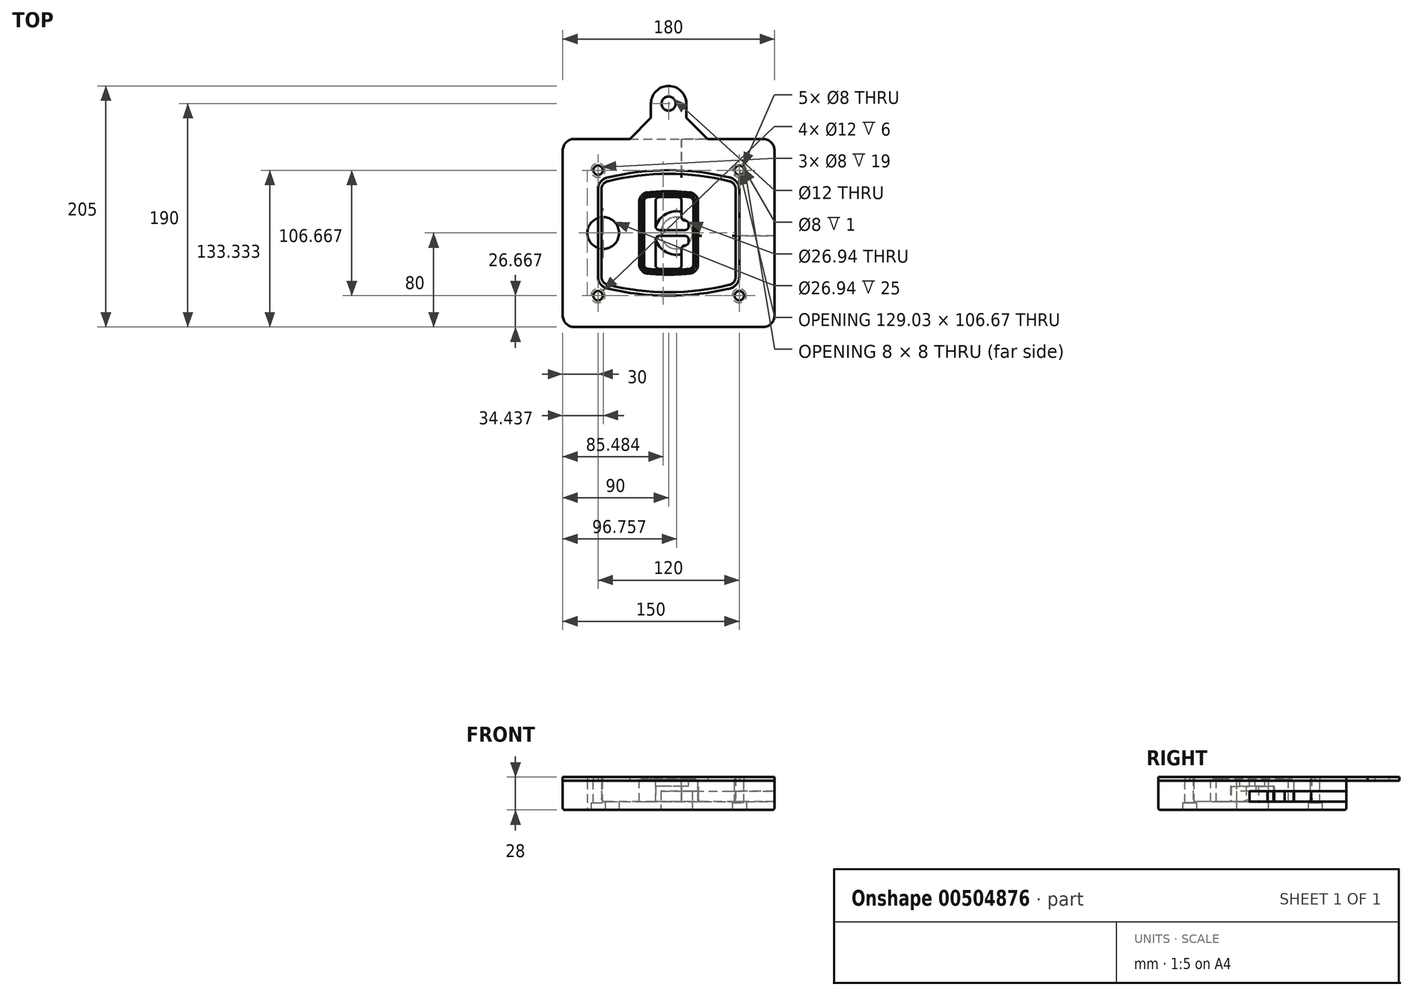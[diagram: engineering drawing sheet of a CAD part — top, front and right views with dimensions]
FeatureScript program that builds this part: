
annotation { "Feature Type Name" : "Feature", "Feature Type Description" : "" }
export const myFeature = defineFeature(function(context is Context, id is Id, definition is map)
    precondition{}
    {
        {
            var Q0;
            Q0=qCreatedBy(makeId("Top.planeOp"),FACE);
            var sketch = newSketch(context, id + "F0", { "sketchPlane" : qUnion([Q0])});
            skPoint(sketch, "E0.rect.middle", {"position": v(0, 0) * mm});
            skLineSegment(sketch, "E1.bottom", {"start": v(-80, -80) * mm, "end": v(80, -80) * mm});
            skLineSegment(sketch, "E1.top", {"start": v(-80, 80) * mm, "end": v(80, 80) * mm});
            skLineSegment(sketch, "E1.left", {"start": v(-90, -70) * mm, "end": v(-90, 70) * mm});
            skLineSegment(sketch, "E1.right", {"start": v(90, -70) * mm, "end": v(90, 70) * mm});
            skLineSegment(sketch, "E2", {"start": v(-90, 80) * mm, "end": v(90, -80) * mm, "construction": true});
            skLineSegment(sketch, "E3", {"start": v(90, 80) * mm, "end": v(-90, -80) * mm, "construction": true});
            skCircle(sketch, "E4", {"center": v(-60, 53.33) * mm, "radius": 4 * mm});
            skCircle(sketch, "E5", {"center": v(60, 53.33) * mm, "radius": 4 * mm});
            skCircle(sketch, "E6", {"center": v(60, -53.33) * mm, "radius": 4 * mm});
            skCircle(sketch, "E7", {"center": v(-60, -53.33) * mm, "radius": 4 * mm});
            skLineSegment(sketch, "E8", {"start": v(-60, 53.33) * mm, "end": v(60, 53.33) * mm, "construction": true});
            skLineSegment(sketch, "E9", {"start": v(60, 53.33) * mm, "end": v(60, -53.33) * mm, "construction": true});
            skLineSegment(sketch, "E10", {"start": v(60, -53.33) * mm, "end": v(-60, -53.33) * mm, "construction": true});
            skLineSegment(sketch, "E11", {"start": v(-60, -53.33) * mm, "end": v(-60, 53.33) * mm, "construction": true});
            skLineSegment(sketch, "E12", {"start": v(-60, 37.3) * mm, "end": v(-60, -37.3) * mm});
            skLineSegment(sketch, "E13", {"start": v(60, 37.3) * mm, "end": v(60, -37.3) * mm});
            skArc(sketch, "E14", {"start": v(52.38, 47.01) * mm, "mid": v(0, 53.33) * mm, "end": v(-52.38, 47.01) * mm});
            skArc(sketch, "E15", {"start": v(-52.38, -47.01) * mm, "mid": v(0, -53.33) * mm, "end": v(52.38, -47.01) * mm});
            skLineSegment(sketch, "E16", {"start": v(-60, 0) * mm, "end": v(60, 0) * mm, "construction": true});
            skPoint(sketch, "E17.visualSharp", {"position": v(-60, -45) * mm});
            skArc(sketch, "E17.filletArc", {"start": v(-60, -37.3) * mm, "mid": v(-57.87, -43.47) * mm, "end": v(-52.38, -47.01) * mm});
            skPoint(sketch, "E18.visualSharp", {"position": v(-60, 45) * mm});
            skArc(sketch, "E18.filletArc", {"start": v(-52.38, 47.01) * mm, "mid": v(-57.87, 43.47) * mm, "end": v(-60, 37.3) * mm});
            skPoint(sketch, "E19.visualSharp", {"position": v(60, 45) * mm});
            skArc(sketch, "E19.filletArc", {"start": v(60, 37.3) * mm, "mid": v(57.87, 43.47) * mm, "end": v(52.38, 47.01) * mm});
            skPoint(sketch, "E20.visualSharp", {"position": v(60, -45) * mm});
            skArc(sketch, "E20.filletArc", {"start": v(52.38, -47.01) * mm, "mid": v(57.87, -43.47) * mm, "end": v(60, -37.3) * mm});
            skPoint(sketch, "E21.visualSharp", {"position": v(-90, 80) * mm});
            skArc(sketch, "E21.filletArc", {"start": v(-80, 80) * mm, "mid": v(-87.07, 77.07) * mm, "end": v(-90, 70) * mm});
            skPoint(sketch, "E22.visualSharp", {"position": v(90, 80) * mm});
            skArc(sketch, "E22.filletArc", {"start": v(90, 70) * mm, "mid": v(87.07, 77.07) * mm, "end": v(80, 80) * mm});
            skPoint(sketch, "E23.visualSharp", {"position": v(90, -80) * mm});
            skArc(sketch, "E23.filletArc", {"start": v(80, -80) * mm, "mid": v(87.07, -77.07) * mm, "end": v(90, -70) * mm});
            skPoint(sketch, "E24.visualSharp", {"position": v(-90, -80) * mm});
            skArc(sketch, "E24.filletArc", {"start": v(-90, -70) * mm, "mid": v(-87.07, -77.07) * mm, "end": v(-80, -80) * mm});
            skArc(sketch, "E25.0", {"start": v(57, 37.3) * mm, "mid": v(55.5, 41.62) * mm, "end": v(51.67, 44.1) * mm});
            skLineSegment(sketch, "E25.1", {"start": v(57, 37.3) * mm, "end": v(57, -37.3) * mm});
            skArc(sketch, "E25.2", {"start": v(51.67, -44.1) * mm, "mid": v(55.5, -41.62) * mm, "end": v(57, -37.3) * mm});
            skArc(sketch, "E25.3", {"start": v(-51.67, -44.1) * mm, "mid": v(0, -50.33) * mm, "end": v(51.67, -44.1) * mm});
            skArc(sketch, "E25.4", {"start": v(-57, -37.3) * mm, "mid": v(-55.5, -41.62) * mm, "end": v(-51.67, -44.1) * mm});
            skArc(sketch, "E25.5", {"start": v(51.67, 44.1) * mm, "mid": v(0, 50.33) * mm, "end": v(-51.67, 44.1) * mm});
            skLineSegment(sketch, "E25.6", {"start": v(-57, 37.3) * mm, "end": v(-57, -37.3) * mm});
            skArc(sketch, "E25.7", {"start": v(-51.67, 44.1) * mm, "mid": v(-55.5, 41.62) * mm, "end": v(-57, 37.3) * mm});
            skArc(sketch, "E26.0", {"start": v(-53.33, 50.9) * mm, "mid": v(-61.01, 45.94) * mm, "end": v(-64, 37.3) * mm});
            skArc(sketch, "E26.1", {"start": v(53.33, 50.9) * mm, "mid": v(0, 57.33) * mm, "end": v(-53.33, 50.9) * mm});
            skArc(sketch, "E26.2", {"start": v(64, 37.3) * mm, "mid": v(61.01, 45.94) * mm, "end": v(53.33, 50.9) * mm});
            skLineSegment(sketch, "E26.3", {"start": v(64, 37.3) * mm, "end": v(64, -37.3) * mm});
            skArc(sketch, "E26.4", {"start": v(53.33, -50.9) * mm, "mid": v(61.01, -45.94) * mm, "end": v(64, -37.3) * mm});
            skLineSegment(sketch, "E26.5", {"start": v(-64, 37.3) * mm, "end": v(-64, -37.3) * mm});
            skArc(sketch, "E26.6", {"start": v(-53.33, -50.9) * mm, "mid": v(0, -57.33) * mm, "end": v(53.33, -50.9) * mm});
            skArc(sketch, "E26.7", {"start": v(-64, -37.3) * mm, "mid": v(-61.01, -45.94) * mm, "end": v(-53.33, -50.9) * mm});
            skSolve(sketch);
        }
        {
            var Q0;
            Q0=makeQuery(id+"F0.imprint","IMPRINT",FACE,{"disambiguationData":[TD([[makeQuery(id+"F0.imprint","IMPRINT",EDGE,{"derivedFrom":sQuery(id+"F0.wireOp",EDGE,"E1.bottom")}),1.0]])]});
            var Q1;
            Q1=makeQuery(id+"F0.imprint","IMPRINT",FACE,{"disambiguationData":[TD([[makeQuery(id+"F0.imprint","IMPRINT",EDGE,{"derivedFrom":sQuery(id+"F0.wireOp",EDGE,"E12")}),1.0]])]});
            var Q2;
            Q2=makeQuery(id+"F0.imprint","IMPRINT",FACE,{"disambiguationData":[TD([[makeQuery(id+"F0.imprint","IMPRINT",EDGE,{"derivedFrom":sQuery(id+"F0.wireOp",EDGE,"E25.0")}),1.0]])]});
            var Q3;
            Q3=makeQuery(id+"F0.imprint","IMPRINT",FACE,{"disambiguationData":[TD([[makeQuery(id+"F0.imprint","IMPRINT",EDGE,{"derivedFrom":sQuery(id+"F0.wireOp",EDGE,"E12")}),-1.0]])]});
            extrude(context, id + "F1", {"entities" : qUnion([Q0, Q1, Q2, Q3]), "oppositeDirection" : true, "depth" : 25 * mm});
        }
        {
            var Q0;
            Q0=makeQuery(id+"F0.imprint","IMPRINT",FACE,{"disambiguationData":[TD([[makeQuery(id+"F0.imprint","IMPRINT",EDGE,{"derivedFrom":sQuery(id+"F0.wireOp",EDGE,"E12")}),1.0]])]});
            extrude(context, id + "F2", {"entities" : qUnion([Q0]), "operationType" : NewBodyOperationType.ADD, "depth" : 3 * mm});
        }
        {
            var Q0;
            Q0=makeQuery(id+"F0.imprint","IMPRINT",FACE,{"disambiguationData":[TD([[makeQuery(id+"F0.imprint","IMPRINT",EDGE,{"derivedFrom":sQuery(id+"F0.wireOp",EDGE,"E25.0")}),1.0]])]});
            extrude(context, id + "F3", {"entities" : qUnion([Q0]), "operationType" : NewBodyOperationType.REMOVE, "oppositeDirection" : true, "depth" : 18 * mm});
        }
        {
            var Q0;
            Q0=makeQuery(id+"F2.opExtrude","CAP_FACE",FACE,{"disambiguationData":[OSD([sQuery(id+"F0.wireOp",EDGE,"E12"),sQuery(id+"F0.wireOp",EDGE,"E13"),sQuery(id+"F0.wireOp",EDGE,"E14"),sQuery(id+"F0.wireOp",EDGE,"E15"),sQuery(id+"F0.wireOp",EDGE,"E17.filletArc"),sQuery(id+"F0.wireOp",EDGE,"E18.filletArc"),sQuery(id+"F0.wireOp",EDGE,"E19.filletArc"),sQuery(id+"F0.wireOp",EDGE,"E20.filletArc"),sQuery(id+"F0.wireOp",EDGE,"E25.0"),sQuery(id+"F0.wireOp",EDGE,"E25.1"),sQuery(id+"F0.wireOp",EDGE,"E25.2"),sQuery(id+"F0.wireOp",EDGE,"E25.3"),sQuery(id+"F0.wireOp",EDGE,"E25.4"),sQuery(id+"F0.wireOp",EDGE,"E25.5"),sQuery(id+"F0.wireOp",EDGE,"E25.6"),sQuery(id+"F0.wireOp",EDGE,"E25.7")])],"isStart":false});
            var sketch = newSketch(context, id + "F4", { "sketchPlane" : qUnion([Q0])});
            skArc(sketch, "E27.0", {"start": v(-17.7, -34.56) * mm, "mid": v(0, -35.33) * mm, "end": v(17.7, -34.56) * mm});
            skArc(sketch, "E28.0", {"start": v(17.7, 34.56) * mm, "mid": v(0, 35.33) * mm, "end": v(-17.7, 34.56) * mm});
            skLineSegment(sketch, "E29", {"start": v(-25, 26.59) * mm, "end": v(-25, -26.59) * mm});
            skLineSegment(sketch, "E30", {"start": v(25, 26.59) * mm, "end": v(25, -26.59) * mm});
            skLineSegment(sketch, "E31", {"start": v(-25, 33.78) * mm, "end": v(25, 33.78) * mm, "construction": true});
            skLineSegment(sketch, "E32", {"start": v(-25, -33.78) * mm, "end": v(25, -33.78) * mm, "construction": true});
            skPoint(sketch, "E33.visualSharp", {"position": v(-25, 33.78) * mm});
            skArc(sketch, "E33.filletArc", {"start": v(-17.7, 34.56) * mm, "mid": v(-22.9, 32) * mm, "end": v(-25, 26.59) * mm});
            skPoint(sketch, "E34.visualSharp", {"position": v(25, 33.78) * mm});
            skArc(sketch, "E34.filletArc", {"start": v(25, 26.59) * mm, "mid": v(22.9, 32) * mm, "end": v(17.7, 34.56) * mm});
            skPoint(sketch, "E35.visualSharp", {"position": v(25, -33.78) * mm});
            skArc(sketch, "E35.filletArc", {"start": v(17.7, -34.56) * mm, "mid": v(22.9, -32) * mm, "end": v(25, -26.59) * mm});
            skPoint(sketch, "E36.visualSharp", {"position": v(-25, -33.78) * mm});
            skArc(sketch, "E36.filletArc", {"start": v(-25, -26.59) * mm, "mid": v(-22.9, -32) * mm, "end": v(-17.7, -34.56) * mm});
            skArc(sketch, "E37.0", {"start": v(51.67, 44.1) * mm, "mid": v(0, 50.33) * mm, "end": v(-51.67, 44.1) * mm});
            skArc(sketch, "E37.1", {"start": v(-51.67, 44.1) * mm, "mid": v(-55.5, 41.62) * mm, "end": v(-57, 37.3) * mm});
            skLineSegment(sketch, "E37.2", {"start": v(-57, 37.3) * mm, "end": v(-57, -37.3) * mm});
            skArc(sketch, "E37.3", {"start": v(-57, -37.3) * mm, "mid": v(-55.5, -41.62) * mm, "end": v(-51.67, -44.1) * mm});
            skArc(sketch, "E37.4", {"start": v(-51.67, -44.1) * mm, "mid": v(0, -50.33) * mm, "end": v(51.67, -44.1) * mm});
            skArc(sketch, "E37.5", {"start": v(51.67, -44.1) * mm, "mid": v(55.5, -41.62) * mm, "end": v(57, -37.3) * mm});
            skLineSegment(sketch, "E37.6", {"start": v(57, 37.3) * mm, "end": v(57, -37.3) * mm});
            skArc(sketch, "E37.7", {"start": v(57, 37.3) * mm, "mid": v(55.5, 41.62) * mm, "end": v(51.67, 44.1) * mm});
            skLineSegment(sketch, "E38.0", {"start": v(23, 26.59) * mm, "end": v(23, -26.59) * mm});
            skArc(sketch, "E38.1", {"start": v(17.53, -32.56) * mm, "mid": v(21.42, -30.64) * mm, "end": v(23, -26.59) * mm});
            skArc(sketch, "E38.2", {"start": v(-17.53, -32.56) * mm, "mid": v(0, -33.33) * mm, "end": v(17.53, -32.56) * mm});
            skArc(sketch, "E38.3", {"start": v(-23, -26.59) * mm, "mid": v(-21.42, -30.64) * mm, "end": v(-17.53, -32.56) * mm});
            skLineSegment(sketch, "E38.4", {"start": v(-23, 26.59) * mm, "end": v(-23, -26.59) * mm});
            skArc(sketch, "E38.5", {"start": v(23, 26.59) * mm, "mid": v(21.42, 30.64) * mm, "end": v(17.53, 32.56) * mm});
            skArc(sketch, "E38.6", {"start": v(-17.53, 32.56) * mm, "mid": v(-21.42, 30.64) * mm, "end": v(-23, 26.59) * mm});
            skArc(sketch, "E38.7", {"start": v(17.53, 32.56) * mm, "mid": v(0, 33.33) * mm, "end": v(-17.53, 32.56) * mm});
            skArc(sketch, "E39.0", {"start": v(21, 26.59) * mm, "mid": v(19.95, 29.29) * mm, "end": v(17.35, 30.57) * mm});
            skLineSegment(sketch, "E39.1", {"start": v(21, 26.59) * mm, "end": v(21, -26.59) * mm});
            skArc(sketch, "E39.2", {"start": v(17.35, -30.57) * mm, "mid": v(19.95, -29.29) * mm, "end": v(21, -26.59) * mm});
            skArc(sketch, "E39.3", {"start": v(-17.35, -30.57) * mm, "mid": v(0, -31.33) * mm, "end": v(17.35, -30.57) * mm});
            skArc(sketch, "E39.4", {"start": v(-21, -26.59) * mm, "mid": v(-19.95, -29.29) * mm, "end": v(-17.35, -30.57) * mm});
            skArc(sketch, "E39.5", {"start": v(17.35, 30.57) * mm, "mid": v(0, 31.33) * mm, "end": v(-17.35, 30.57) * mm});
            skLineSegment(sketch, "E39.6", {"start": v(-21, 26.59) * mm, "end": v(-21, -26.59) * mm});
            skArc(sketch, "E39.7", {"start": v(-17.35, 30.57) * mm, "mid": v(-19.95, 29.29) * mm, "end": v(-21, 26.59) * mm});
            skLineSegment(sketch, "E40", {"start": v(-25, 0) * mm, "end": v(25, 0) * mm, "construction": true});
            skLineSegment(sketch, "E41", {"start": v(-11, 5.5) * mm, "end": v(-11, 27.5) * mm});
            skLineSegment(sketch, "E42", {"start": v(-8, 30.5) * mm, "end": v(8, 30.5) * mm});
            skLineSegment(sketch, "E43", {"start": v(11, 27.5) * mm, "end": v(11, 13.5) * mm});
            skLineSegment(sketch, "E44", {"start": v(14, 10.5) * mm, "end": v(14, 10.5) * mm});
            skLineSegment(sketch, "E45", {"start": v(17, 7.5) * mm, "end": v(17, 5.5) * mm});
            skLineSegment(sketch, "E46", {"start": v(14, 2.5) * mm, "end": v(-8, 2.5) * mm});
            skPoint(sketch, "E47.visualSharp", {"position": v(-11, 30.5) * mm});
            skArc(sketch, "E47.filletArc", {"start": v(-8, 30.5) * mm, "mid": v(-10.12, 29.62) * mm, "end": v(-11, 27.5) * mm});
            skPoint(sketch, "E48.visualSharp", {"position": v(11, 30.5) * mm});
            skArc(sketch, "E48.filletArc", {"start": v(11, 27.5) * mm, "mid": v(10.12, 29.62) * mm, "end": v(8, 30.5) * mm});
            skPoint(sketch, "E49.visualSharp", {"position": v(11, 10.5) * mm});
            skArc(sketch, "E49.filletArc", {"start": v(11, 13.5) * mm, "mid": v(11.88, 11.38) * mm, "end": v(14, 10.5) * mm});
            skPoint(sketch, "E50.visualSharp", {"position": v(17, 10.5) * mm});
            skArc(sketch, "E50.filletArc", {"start": v(17, 7.5) * mm, "mid": v(16.12, 9.62) * mm, "end": v(14, 10.5) * mm});
            skPoint(sketch, "E51.visualSharp", {"position": v(17, 2.5) * mm});
            skArc(sketch, "E51.filletArc", {"start": v(14, 2.5) * mm, "mid": v(16.12, 3.38) * mm, "end": v(17, 5.5) * mm});
            skPoint(sketch, "E52.visualSharp", {"position": v(-11, 2.5) * mm});
            skArc(sketch, "E52.filletArc", {"start": v(-11, 5.5) * mm, "mid": v(-10.12, 3.38) * mm, "end": v(-8, 2.5) * mm});
            skLineSegment(sketch, "E53.0.MirrorCS", {"start": v(14, -2.5) * mm, "end": v(-8, -2.5) * mm});
            skArc(sketch, "E54.0.MirrorCS", {"start": v(-11, -5.5) * mm, "mid": v(-10.12, -3.38) * mm, "end": v(-8, -2.5) * mm});
            skLineSegment(sketch, "E55.0.MirrorCS", {"start": v(-11, -5.5) * mm, "end": v(-11, -27.5) * mm});
            skArc(sketch, "E56.0.MirrorCS", {"start": v(-8, -30.5) * mm, "mid": v(-10.12, -29.62) * mm, "end": v(-11, -27.5) * mm});
            skLineSegment(sketch, "E57.0.MirrorCS", {"start": v(-8, -30.5) * mm, "end": v(8, -30.5) * mm});
            skArc(sketch, "E58.0.MirrorCS", {"start": v(11, -27.5) * mm, "mid": v(10.12, -29.62) * mm, "end": v(8, -30.5) * mm});
            skLineSegment(sketch, "E59.0.MirrorCS", {"start": v(11, -27.5) * mm, "end": v(11, -13.5) * mm});
            skArc(sketch, "E60.0.MirrorCS", {"start": v(11, -13.5) * mm, "mid": v(11.88, -11.38) * mm, "end": v(14, -10.5) * mm});
            skArc(sketch, "E61.0.MirrorCS", {"start": v(17, -7.5) * mm, "mid": v(16.12, -9.62) * mm, "end": v(14, -10.5) * mm});
            skLineSegment(sketch, "E62.0.MirrorCS", {"start": v(17, -7.5) * mm, "end": v(17, -5.5) * mm});
            skArc(sketch, "E63.0.MirrorCS", {"start": v(14, -2.5) * mm, "mid": v(16.12, -3.38) * mm, "end": v(17, -5.5) * mm});
            skSolve(sketch);
        }
        {
            var Q0;
            Q0=makeQuery(id+"F4.imprint","IMPRINT",FACE,{"disambiguationData":[TD([[makeQuery(id+"F4.imprint","IMPRINT",EDGE,{"derivedFrom":sQuery(id+"F4.wireOp",EDGE,"E27.0")}),1.0]])]});
            var Q1;
            Q1=makeQuery(id+"F4.imprint","IMPRINT",FACE,{"disambiguationData":[TD([[makeQuery(id+"F4.imprint","IMPRINT",EDGE,{"derivedFrom":sQuery(id+"F4.wireOp",EDGE,"E38.0")}),-1.0]])]});
            var Q2;
            Q2=makeQuery(id+"F4.imprint","IMPRINT",FACE,{"disambiguationData":[TD([[makeQuery(id+"F4.imprint","IMPRINT",EDGE,{"derivedFrom":sQuery(id+"F4.wireOp",EDGE,"E39.0")}),1.0]])]});
            extrude(context, id + "F5", {"entities" : qUnion([Q0, Q1, Q2]), "operationType" : NewBodyOperationType.ADD, "endBound" : BoundingType.UP_TO_NEXT, "oppositeDirection" : true, "depth" : 25 * mm});
        }
        {
            var Q0;
            Q0=makeQuery(id+"F4.imprint","IMPRINT",FACE,{"disambiguationData":[TD([[makeQuery(id+"F4.imprint","IMPRINT",EDGE,{"derivedFrom":sQuery(id+"F4.wireOp",EDGE,"E38.0")}),-1.0]])]});
            extrude(context, id + "F6", {"entities" : qUnion([Q0]), "operationType" : NewBodyOperationType.REMOVE, "oppositeDirection" : true, "depth" : 2 * mm});
        }
        {
            var Q0;
            Q0=makeQuery(id+"F1.opExtrude","CAP_FACE",FACE,{"disambiguationData":[OSD([sQuery(id+"F0.wireOp",EDGE,"E1.bottom"),sQuery(id+"F0.wireOp",EDGE,"E1.top"),sQuery(id+"F0.wireOp",EDGE,"E1.left"),sQuery(id+"F0.wireOp",EDGE,"E1.right"),sQuery(id+"F0.wireOp",EDGE,"E4"),sQuery(id+"F0.wireOp",EDGE,"E5"),sQuery(id+"F0.wireOp",EDGE,"E6"),sQuery(id+"F0.wireOp",EDGE,"E7"),sQuery(id+"F0.wireOp",EDGE,"E21.filletArc"),sQuery(id+"F0.wireOp",EDGE,"E22.filletArc"),sQuery(id+"F0.wireOp",EDGE,"E23.filletArc"),sQuery(id+"F0.wireOp",EDGE,"E24.filletArc")])],"isStart":false});
            var sketch = newSketch(context, id + "F7", { "sketchPlane" : qUnion([Q0])});
            skCircle(sketch, "E64", {"center": v(6.76, 0) * mm, "radius": 13.47 * mm});
            skCircle(sketch, "E65", {"center": v(-55.56, 0) * mm, "radius": 13.47 * mm});
            skLineSegment(sketch, "E66", {"start": v(90, 0) * mm, "end": v(-90, 0) * mm});
            skCircle(sketch, "E67", {"center": v(6.76, 0) * mm, "radius": 18.47 * mm});
            skCircle(sketch, "E68", {"center": v(60, -53.33) * mm, "radius": 6 * mm});
            skCircle(sketch, "E69", {"center": v(-60, -53.33) * mm, "radius": 6 * mm});
            skCircle(sketch, "E70", {"center": v(-60, 53.33) * mm, "radius": 6 * mm});
            skCircle(sketch, "E71", {"center": v(60, 53.33) * mm, "radius": 6 * mm});
            skSolve(sketch);
        }
        {
            var Q0;
            {var subQ1=sQuery(id+"F7.wireOp",EDGE,"E66");var subQ4=sQuery(id+"F7.wireOp",EDGE,"E64");var subQ6=makeQuery(id+"F7.imprint","INTERSECT",VERTEX,{"disambiguationData":[OD(0.0)],"derivedFrom":[subQ4,subQ1]});Q0=makeQuery(id+"F7.imprint","IMPRINT",FACE,{"disambiguationData":[TD([[makeQuery(id+"F7.imprint","IMPRINT",EDGE,{"disambiguationData":[TD([[subQ6,-1.0]])],"derivedFrom":subQ4}),-1.0]])]});}
            var Q1;
            {var subQ0=sQuery(id+"F7.wireOp",EDGE,"E66");var subQ1=sQuery(id+"F7.wireOp",EDGE,"E64");var subQ3=makeQuery(id+"F7.imprint","INTERSECT",VERTEX,{"disambiguationData":[OD(0.0)],"derivedFrom":[subQ1,subQ0]});Q1=makeQuery(id+"F7.imprint","IMPRINT",FACE,{"disambiguationData":[TD([[makeQuery(id+"F7.imprint","IMPRINT",EDGE,{"disambiguationData":[TD([[subQ3,-1.0]])],"derivedFrom":subQ1}),1.0]])]});}
            var Q2;
            {var subQ0=sQuery(id+"F7.wireOp",EDGE,"E66");var subQ1=sQuery(id+"F7.wireOp",EDGE,"E64");var subQ3=makeQuery(id+"F7.imprint","INTERSECT",VERTEX,{"disambiguationData":[OD(0.0)],"derivedFrom":[subQ1,subQ0]});Q2=makeQuery(id+"F7.imprint","IMPRINT",FACE,{"disambiguationData":[TD([[makeQuery(id+"F7.imprint","IMPRINT",EDGE,{"disambiguationData":[TD([[subQ3,1.0]])],"derivedFrom":subQ1}),1.0]])]});}
            var Q3;
            {var subQ1=sQuery(id+"F7.wireOp",EDGE,"E66");var subQ4=sQuery(id+"F7.wireOp",EDGE,"E64");var subQ6=makeQuery(id+"F7.imprint","INTERSECT",VERTEX,{"disambiguationData":[OD(0.0)],"derivedFrom":[subQ4,subQ1]});Q3=makeQuery(id+"F7.imprint","IMPRINT",FACE,{"disambiguationData":[TD([[makeQuery(id+"F7.imprint","IMPRINT",EDGE,{"disambiguationData":[TD([[subQ6,1.0]])],"derivedFrom":subQ4}),-1.0]])]});}
            extrude(context, id + "F8", {"entities" : qUnion([Q0, Q1, Q2, Q3]), "operationType" : NewBodyOperationType.ADD, "oppositeDirection" : true, "depth" : 20 * mm});
        }
        {
            var Q0;
            {var subQ0=sQuery(id+"F7.wireOp",EDGE,"E66");var subQ1=sQuery(id+"F7.wireOp",EDGE,"E64");var subQ3=makeQuery(id+"F7.imprint","INTERSECT",VERTEX,{"disambiguationData":[OD(0.0)],"derivedFrom":[subQ1,subQ0]});Q0=makeQuery(id+"F7.imprint","IMPRINT",FACE,{"disambiguationData":[TD([[makeQuery(id+"F7.imprint","IMPRINT",EDGE,{"disambiguationData":[TD([[subQ3,-1.0]])],"derivedFrom":subQ1}),1.0]])]});}
            var Q1;
            {var subQ0=sQuery(id+"F7.wireOp",EDGE,"E66");var subQ1=sQuery(id+"F7.wireOp",EDGE,"E64");var subQ3=makeQuery(id+"F7.imprint","INTERSECT",VERTEX,{"disambiguationData":[OD(0.0)],"derivedFrom":[subQ1,subQ0]});Q1=makeQuery(id+"F7.imprint","IMPRINT",FACE,{"disambiguationData":[TD([[makeQuery(id+"F7.imprint","IMPRINT",EDGE,{"disambiguationData":[TD([[subQ3,1.0]])],"derivedFrom":subQ1}),1.0]])]});}
            extrude(context, id + "F9", {"entities" : qUnion([Q0, Q1]), "operationType" : NewBodyOperationType.REMOVE, "oppositeDirection" : true, "depth" : 16 * mm});
        }
        {
            var Q0;
            {var subQ0=sQuery(id+"F7.wireOp",EDGE,"E66");var subQ1=sQuery(id+"F7.wireOp",EDGE,"E65");var subQ3=makeQuery(id+"F7.imprint","INTERSECT",VERTEX,{"disambiguationData":[OD(0.0)],"derivedFrom":[subQ1,subQ0]});Q0=makeQuery(id+"F7.imprint","IMPRINT",FACE,{"disambiguationData":[TD([[makeQuery(id+"F7.imprint","IMPRINT",EDGE,{"disambiguationData":[TD([[subQ3,-1.0]])],"derivedFrom":subQ1}),1.0]])]});}
            var Q1;
            {var subQ0=sQuery(id+"F7.wireOp",EDGE,"E66");var subQ1=sQuery(id+"F7.wireOp",EDGE,"E65");var subQ3=makeQuery(id+"F7.imprint","INTERSECT",VERTEX,{"disambiguationData":[OD(0.0)],"derivedFrom":[subQ1,subQ0]});Q1=makeQuery(id+"F7.imprint","IMPRINT",FACE,{"disambiguationData":[TD([[makeQuery(id+"F7.imprint","IMPRINT",EDGE,{"disambiguationData":[TD([[subQ3,1.0]])],"derivedFrom":subQ1}),1.0]])]});}
            extrude(context, id + "F10", {"entities" : qUnion([Q0, Q1]), "operationType" : NewBodyOperationType.REMOVE, "oppositeDirection" : true, "depth" : 25 * mm});
        }
        {
            var Q0;
            Q0=makeQuery(id+"F7.imprint","IMPRINT",FACE,{"disambiguationData":[TD([[makeQuery(id+"F7.imprint","IMPRINT",EDGE,{"derivedFrom":sQuery(id+"F7.wireOp",EDGE,"E68")}),1.0]])]});
            var Q1;
            Q1=makeQuery(id+"F7.imprint","IMPRINT",FACE,{"disambiguationData":[TD([[makeQuery(id+"F7.imprint","IMPRINT",EDGE,{"derivedFrom":makeQuery(id+"F1.opExtrude","CAP_EDGE",EDGE,{"disambiguationData":[OSD([sQuery(id+"F0.wireOp",EDGE,"E5")])],"isStart":false})}),-1.0]])]});
            var Q2;
            Q2=makeQuery(id+"F7.imprint","IMPRINT",FACE,{"disambiguationData":[TD([[makeQuery(id+"F7.imprint","IMPRINT",EDGE,{"derivedFrom":sQuery(id+"F7.wireOp",EDGE,"E69")}),1.0]])]});
            var Q3;
            Q3=makeQuery(id+"F7.imprint","IMPRINT",FACE,{"disambiguationData":[TD([[makeQuery(id+"F7.imprint","IMPRINT",EDGE,{"derivedFrom":makeQuery(id+"F1.opExtrude","CAP_EDGE",EDGE,{"disambiguationData":[OSD([sQuery(id+"F0.wireOp",EDGE,"E4")])],"isStart":false})}),-1.0]])]});
            var Q4;
            Q4=makeQuery(id+"F7.imprint","IMPRINT",FACE,{"disambiguationData":[TD([[makeQuery(id+"F7.imprint","IMPRINT",EDGE,{"derivedFrom":sQuery(id+"F7.wireOp",EDGE,"E70")}),1.0]])]});
            var Q5;
            Q5=makeQuery(id+"F7.imprint","IMPRINT",FACE,{"disambiguationData":[TD([[makeQuery(id+"F7.imprint","IMPRINT",EDGE,{"derivedFrom":makeQuery(id+"F1.opExtrude","CAP_EDGE",EDGE,{"disambiguationData":[OSD([sQuery(id+"F0.wireOp",EDGE,"E7")])],"isStart":false})}),-1.0]])]});
            var Q6;
            Q6=makeQuery(id+"F7.imprint","IMPRINT",FACE,{"disambiguationData":[TD([[makeQuery(id+"F7.imprint","IMPRINT",EDGE,{"derivedFrom":sQuery(id+"F7.wireOp",EDGE,"E71")}),1.0]])]});
            var Q7;
            Q7=makeQuery(id+"F7.imprint","IMPRINT",FACE,{"disambiguationData":[TD([[makeQuery(id+"F7.imprint","IMPRINT",EDGE,{"derivedFrom":makeQuery(id+"F1.opExtrude","CAP_EDGE",EDGE,{"disambiguationData":[OSD([sQuery(id+"F0.wireOp",EDGE,"E6")])],"isStart":false})}),-1.0]])]});
            extrude(context, id + "F11", {"entities" : qUnion([Q0, Q1, Q2, Q3, Q4, Q5, Q6, Q7]), "operationType" : NewBodyOperationType.REMOVE, "oppositeDirection" : true, "depth" : 6 * mm});
        }
        {
            var Q0;
            Q0=makeQuery(id+"F9.boolean.opBoolean","COPY",FACE,{"derivedFrom":makeQuery(id+"F9.opExtrude","CAP_FACE",FACE,{"disambiguationData":[OSD([sQuery(id+"F7.wireOp",EDGE,"E64")])],"isStart":false})});
            var sketch = newSketch(context, id + "F12", { "sketchPlane" : qUnion([Q0])});
            skArc(sketch, "E72.0", {"start": v(11, -88.19) * mm, "mid": v(97.1, -83.6) * mm, "end": v(92.5, 2.5) * mm});
            skLineSegment(sketch, "E72.1", {"start": v(11, -17.97) * mm, "end": v(11, -17.97) * mm});
            skLineSegment(sketch, "E73", {"start": v(92.5, -105.13) * mm, "end": v(102.3, -105.13) * mm});
            skLineSegment(sketch, "E74.0", {"start": v(92.5, 2.5) * mm, "end": v(14, 2.5) * mm});
            skArc(sketch, "E74.1", {"start": v(14, 2.5) * mm, "mid": v(16.12, 3.38) * mm, "end": v(17, 5.5) * mm});
            skLineSegment(sketch, "E74.2", {"start": v(17, 7.5) * mm, "end": v(17, 5.5) * mm});
            skArc(sketch, "E74.3", {"start": v(17, 7.5) * mm, "mid": v(16.12, 9.62) * mm, "end": v(14, 10.5) * mm});
            skArc(sketch, "E74.4", {"start": v(11, 13.5) * mm, "mid": v(11.88, 11.38) * mm, "end": v(14, 10.5) * mm});
            skLineSegment(sketch, "E74.5", {"start": v(11, 13.5) * mm, "end": v(11, -88.19) * mm});
            skLineSegment(sketch, "E74.7", {"start": v(92.5, -2.5) * mm, "end": v(14, -2.5) * mm});
            skArc(sketch, "E74.8", {"start": v(14, -2.5) * mm, "mid": v(16.12, -3.38) * mm, "end": v(17, -5.5) * mm});
            skLineSegment(sketch, "E74.9", {"start": v(17, -7.5) * mm, "end": v(17, -5.5) * mm});
            skArc(sketch, "E74.10", {"start": v(17, -7.5) * mm, "mid": v(16.12, -9.62) * mm, "end": v(14, -10.5) * mm});
            skArc(sketch, "E74.11", {"start": v(11, -13.5) * mm, "mid": v(11.88, -11.38) * mm, "end": v(14, -10.5) * mm});
            skLineSegment(sketch, "E74.12", {"start": v(11, -17.97) * mm, "end": v(11, -13.5) * mm});
            skPoint(sketch, "E75.orphan", {"position": v(11, -27.5) * mm});
            skPoint(sketch, "E76.orphan", {"position": v(-8, -2.5) * mm});
            skPoint(sketch, "E77.orphan", {"position": v(-8, 2.5) * mm});
            skPoint(sketch, "E78.orphan", {"position": v(11, 27.5) * mm});
            skSolve(sketch);
        }
        {
            var Q0;
            {var subQ7=sQuery(id+"F12.wireOp",EDGE,"E72.0");var subQ14=sQuery(id+"F12.wireOp",EDGE,"E72.1");var subQ16=sQuery(id+"F12.wireOp",EDGE,"E74.1");var subQ18=sQuery(id+"F12.wireOp",EDGE,"E74.8");Q0=qUnion([makeQuery(id+"F12.imprint","IMPRINT",FACE,{"disambiguationData":[TD([[makeQuery(id+"F12.imprint","IMPRINT",EDGE,{"derivedFrom":subQ7}),1.0]])]}),makeQuery(id+"F12.imprint","IMPRINT",FACE,{"disambiguationData":[TD([[makeQuery(id+"F12.imprint","IMPRINT",EDGE,{"derivedFrom":subQ14}),1.0]])]}),makeQuery(id+"F12.imprint","IMPRINT",FACE,{"disambiguationData":[TD([[makeQuery(id+"F12.imprint","IMPRINT",EDGE,{"derivedFrom":subQ16}),1.0]])]}),makeQuery(id+"F12.imprint","IMPRINT",FACE,{"disambiguationData":[TD([[makeQuery(id+"F12.imprint","IMPRINT",EDGE,{"derivedFrom":subQ18}),-1.0]])]})]);}
            var Q1;
            Q1=makeQuery(id+"F5.boolean.opBoolean","SPLIT",FACE,{"disambiguationData":[TD([makeQuery(id+"F5.opExtrude","SWEPT_FACE",FACE,{"disambiguationData":[OSD([sQuery(id+"F4.wireOp",EDGE,"E41")])]})])],"derivedFrom":makeQuery(id+"F3.boolean.opBoolean","COPY",FACE,{"derivedFrom":makeQuery(id+"F3.opExtrude","CAP_FACE",FACE,{"disambiguationData":[OSD([sQuery(id+"F0.wireOp",EDGE,"E25.0"),sQuery(id+"F0.wireOp",EDGE,"E25.1"),sQuery(id+"F0.wireOp",EDGE,"E25.2"),sQuery(id+"F0.wireOp",EDGE,"E25.3"),sQuery(id+"F0.wireOp",EDGE,"E25.4"),sQuery(id+"F0.wireOp",EDGE,"E25.5"),sQuery(id+"F0.wireOp",EDGE,"E25.6"),sQuery(id+"F0.wireOp",EDGE,"E25.7")])],"isStart":false})})});
            extrude(context, id + "F13", {"entities" : qUnion([Q0]), "operationType" : NewBodyOperationType.REMOVE, "endBound" : BoundingType.UP_TO_SURFACE, "endBoundEntityFace" : qUnion([Q1]), "depth" : 25 * mm});
        }
        {
            var Q0;
            Q0=makeQuery(id+"F3.boolean.opBoolean","COPY",EDGE,{"derivedFrom":makeQuery(id+"F3.opExtrude","CAP_EDGE",EDGE,{"disambiguationData":[OSD([sQuery(id+"F0.wireOp",EDGE,"E25.6")])],"isStart":false})});
            var Q1;
            Q1=makeQuery(id+"F8.boolean.opBoolean","INTERSECT",EDGE,{"derivedFrom":[makeQuery(id+"F5.opExtrude","SWEPT_FACE",FACE,{"disambiguationData":[OSD([sQuery(id+"F4.wireOp",EDGE,"E30")])]}),makeQuery(id+"F8.opExtrude","CAP_FACE",FACE,{"disambiguationData":[OSD([sQuery(id+"F7.wireOp",EDGE,"E67")])],"isStart":false})]});
            var Q2;
            Q2=makeQuery(id+"F8.boolean.opBoolean","INTERSECT",EDGE,{"disambiguationData":[OD(1.0)],"derivedFrom":[makeQuery(id+"F5.opExtrude","SWEPT_FACE",FACE,{"disambiguationData":[OSD([sQuery(id+"F4.wireOp",EDGE,"E30")])]}),makeQuery(id+"F8.opExtrude","SWEPT_FACE",FACE,{"disambiguationData":[OSD([sQuery(id+"F7.wireOp",EDGE,"E67")])]})]});
            var Q3;
            {var subQ0=makeQuery(id+"F3.boolean.opBoolean","COPY",FACE,{"derivedFrom":makeQuery(id+"F3.opExtrude","CAP_FACE",FACE,{"disambiguationData":[OSD([sQuery(id+"F0.wireOp",EDGE,"E25.0"),sQuery(id+"F0.wireOp",EDGE,"E25.1"),sQuery(id+"F0.wireOp",EDGE,"E25.2"),sQuery(id+"F0.wireOp",EDGE,"E25.3"),sQuery(id+"F0.wireOp",EDGE,"E25.4"),sQuery(id+"F0.wireOp",EDGE,"E25.5"),sQuery(id+"F0.wireOp",EDGE,"E25.6"),sQuery(id+"F0.wireOp",EDGE,"E25.7")])],"isStart":false})});var subQ1=sQuery(id+"F4.wireOp",EDGE,"E30");Q3=makeQuery(id+"F8.boolean.opBoolean","SPLIT",EDGE,{"disambiguationData":[TD([makeQuery(id+"F5.opExtrude","SWEPT_FACE",FACE,{"disambiguationData":[OSD([sQuery(id+"F4.wireOp",EDGE,"E35.filletArc")])]})])],"derivedFrom":makeQuery(id+"F5.opExtrude","TWEAK_EDGE",EDGE,{"derivedFrom":[subQ0,makeQuery(id+"F4.imprint","IMPRINT",EDGE,{"derivedFrom":subQ1})]})});}
            var Q4;
            {var subQ0=sQuery(id+"F0.wireOp",EDGE,"E25.0");var subQ1=sQuery(id+"F0.wireOp",EDGE,"E25.1");var subQ2=sQuery(id+"F0.wireOp",EDGE,"E25.2");var subQ3=sQuery(id+"F0.wireOp",EDGE,"E25.3");var subQ4=sQuery(id+"F0.wireOp",EDGE,"E25.4");var subQ5=sQuery(id+"F0.wireOp",EDGE,"E25.5");var subQ6=sQuery(id+"F0.wireOp",EDGE,"E25.6");var subQ7=sQuery(id+"F0.wireOp",EDGE,"E25.7");Q4=makeQuery(id+"F8.boolean.opBoolean","INTERSECT",EDGE,{"derivedFrom":[makeQuery(id+"F5.boolean.opBoolean","SPLIT",FACE,{"disambiguationData":[TD([makeQuery(id+"F2.opExtrude","SWEPT_FACE",FACE,{"disambiguationData":[OSD([subQ0])]})])],"derivedFrom":makeQuery(id+"F3.boolean.opBoolean","COPY",FACE,{"derivedFrom":makeQuery(id+"F3.opExtrude","CAP_FACE",FACE,{"disambiguationData":[OSD([subQ0,subQ1,subQ2,subQ3,subQ4,subQ5,subQ6,subQ7])],"isStart":false})})}),makeQuery(id+"F8.opExtrude","SWEPT_FACE",FACE,{"disambiguationData":[OSD([sQuery(id+"F7.wireOp",EDGE,"E67")])]})]});}
            var Q5;
            Q5=makeQuery(id+"F8.boolean.opBoolean","INTERSECT",EDGE,{"disambiguationData":[OD(0.0)],"derivedFrom":[makeQuery(id+"F5.opExtrude","SWEPT_FACE",FACE,{"disambiguationData":[OSD([sQuery(id+"F4.wireOp",EDGE,"E30")])]}),makeQuery(id+"F8.opExtrude","SWEPT_FACE",FACE,{"disambiguationData":[OSD([sQuery(id+"F7.wireOp",EDGE,"E67")])]})]});
            fillet(context, id + "F14", {"entities" : qUnion([Q0, Q1, Q2, Q3, Q4, Q5]), "radius" : 3 * mm, "tangentPropagation" : true, "allowEdgeOverflow" : false});
        }
        {
            var Q0;
            Q0=makeQuery(id+"F1.opExtrude","CAP_EDGE",EDGE,{"disambiguationData":[OSD([sQuery(id+"F0.wireOp",EDGE,"E1.bottom")])],"isStart":false});
            fillet(context, id + "F15", {"entities" : qUnion([Q0]), "radius" : 2 * mm, "tangentPropagation" : true, "allowEdgeOverflow" : false});
        }
        {
            var Q0;
            {var subQ0=sQuery(id+"F0.wireOp",EDGE,"E21.filletArc");var subQ1=sQuery(id+"F0.wireOp",EDGE,"E7");var subQ2=sQuery(id+"F0.wireOp",EDGE,"E6");var subQ3=sQuery(id+"F0.wireOp",EDGE,"E5");var subQ4=sQuery(id+"F0.wireOp",EDGE,"E4");var subQ5=sQuery(id+"F0.wireOp",EDGE,"E22.filletArc");var subQ6=sQuery(id+"F0.wireOp",EDGE,"E1.bottom");var subQ7=sQuery(id+"F0.wireOp",EDGE,"E1.right");var subQ8=sQuery(id+"F0.wireOp",EDGE,"E1.top");var subQ9=sQuery(id+"F0.wireOp",EDGE,"E1.left");var subQ10=sQuery(id+"F0.wireOp",EDGE,"E23.filletArc");var subQ11=sQuery(id+"F0.wireOp",EDGE,"E24.filletArc");Q0=makeQuery(id+"F2.boolean.opBoolean","SPLIT",FACE,{"disambiguationData":[TD([makeQuery(id+"F1.opExtrude","SWEPT_FACE",FACE,{"disambiguationData":[OSD([subQ6])]})])],"derivedFrom":makeQuery(id+"F1.opExtrude","CAP_FACE",FACE,{"disambiguationData":[OSD([subQ6,subQ8,subQ9,subQ7,subQ4,subQ3,subQ2,subQ1,subQ0,subQ5,subQ10,subQ11])],"isStart":true})});}
            var sketch = newSketch(context, id + "F16", { "sketchPlane" : qUnion([Q0])});
            skLineSegment(sketch, "E79", {"start": v(0, 80) * mm, "end": v(0, 110) * mm, "construction": true});
            skArc(sketch, "E80", {"start": v(15, 110) * mm, "mid": v(0, 125) * mm, "end": v(-15, 110) * mm});
            skLineSegment(sketch, "E81", {"start": v(-15, 110) * mm, "end": v(-15, 98) * mm});
            skLineSegment(sketch, "E82", {"start": v(-15, 98) * mm, "end": v(-33, 80) * mm});
            skLineSegment(sketch, "E83", {"start": v(15, 110) * mm, "end": v(15, 98) * mm});
            skLineSegment(sketch, "E84", {"start": v(15, 98) * mm, "end": v(33, 80) * mm});
            skCircle(sketch, "E85", {"center": v(0, 110) * mm, "radius": 6 * mm});
            skLineSegment(sketch, "E86", {"start": v(-90, 0) * mm, "end": v(90, 0) * mm, "construction": true});
            skLineSegment(sketch, "E87.MirrorCS", {"start": v(-15, -98) * mm, "end": v(-33, -80) * mm});
            skLineSegment(sketch, "E88.MirrorCS", {"start": v(-15, -110) * mm, "end": v(-15, -98) * mm});
            skLineSegment(sketch, "E89.MirrorCS", {"start": v(15, -110) * mm, "end": v(15, -98) * mm});
            skCircle(sketch, "E90.MirrorC", {"center": v(0, -110) * mm, "radius": 6 * mm});
            skArc(sketch, "E91.MirrorCS", {"start": v(15, -110) * mm, "mid": v(0, -125) * mm, "end": v(-15, -110) * mm});
            skLineSegment(sketch, "E92.MirrorCS", {"start": v(0, -80) * mm, "end": v(0, -110) * mm, "construction": true});
            skLineSegment(sketch, "E93.MirrorCS", {"start": v(15, -98) * mm, "end": v(33, -80) * mm});
            skSolve(sketch);
        }
        {
            var Q0;
            Q0=makeQuery(id+"F16.imprint","IMPRINT",FACE,{"disambiguationData":[TD([[makeQuery(id+"F16.imprint","IMPRINT",EDGE,{"derivedFrom":sQuery(id+"F16.wireOp",EDGE,"E80")}),1.0]])]});
            var Q1;
            Q1=makeQuery(id+"F16.imprint","IMPRINT",FACE,{"disambiguationData":[TD([[makeQuery(id+"F16.imprint","IMPRINT",EDGE,{"derivedFrom":sQuery(id+"F16.wireOp",EDGE,"E91.MirrorCS")}),-1.0]])]});
            var Q2;
            {var subQ15=sQuery(id+"F0.wireOp",EDGE,"E1.left");Q2=makeQuery(id+"F16.imprint","IMPRINT",FACE,{"disambiguationData":[TD([[makeQuery(id+"F16.imprint","IMPRINT",EDGE,{"derivedFrom":makeQuery(id+"F1.opExtrude","CAP_EDGE",EDGE,{"disambiguationData":[OSD([subQ15])],"isStart":true})}),-1.0]])]});}
            var Q3;
            Q3=makeQuery(id+"F2.opExtrude","CAP_FACE",FACE,{"disambiguationData":[OSD([sQuery(id+"F0.wireOp",EDGE,"E12"),sQuery(id+"F0.wireOp",EDGE,"E13"),sQuery(id+"F0.wireOp",EDGE,"E14"),sQuery(id+"F0.wireOp",EDGE,"E15"),sQuery(id+"F0.wireOp",EDGE,"E17.filletArc"),sQuery(id+"F0.wireOp",EDGE,"E18.filletArc"),sQuery(id+"F0.wireOp",EDGE,"E19.filletArc"),sQuery(id+"F0.wireOp",EDGE,"E20.filletArc"),sQuery(id+"F0.wireOp",EDGE,"E25.0"),sQuery(id+"F0.wireOp",EDGE,"E25.1"),sQuery(id+"F0.wireOp",EDGE,"E25.2"),sQuery(id+"F0.wireOp",EDGE,"E25.3"),sQuery(id+"F0.wireOp",EDGE,"E25.4"),sQuery(id+"F0.wireOp",EDGE,"E25.5"),sQuery(id+"F0.wireOp",EDGE,"E25.6"),sQuery(id+"F0.wireOp",EDGE,"E25.7")])],"isStart":false});
            extrude(context, id + "F17", {"entities" : qUnion([Q0, Q1, Q2]), "endBound" : BoundingType.UP_TO_SURFACE, "endBoundEntityFace" : qUnion([Q3]), "depth" : 25 * mm});
        }
    });
